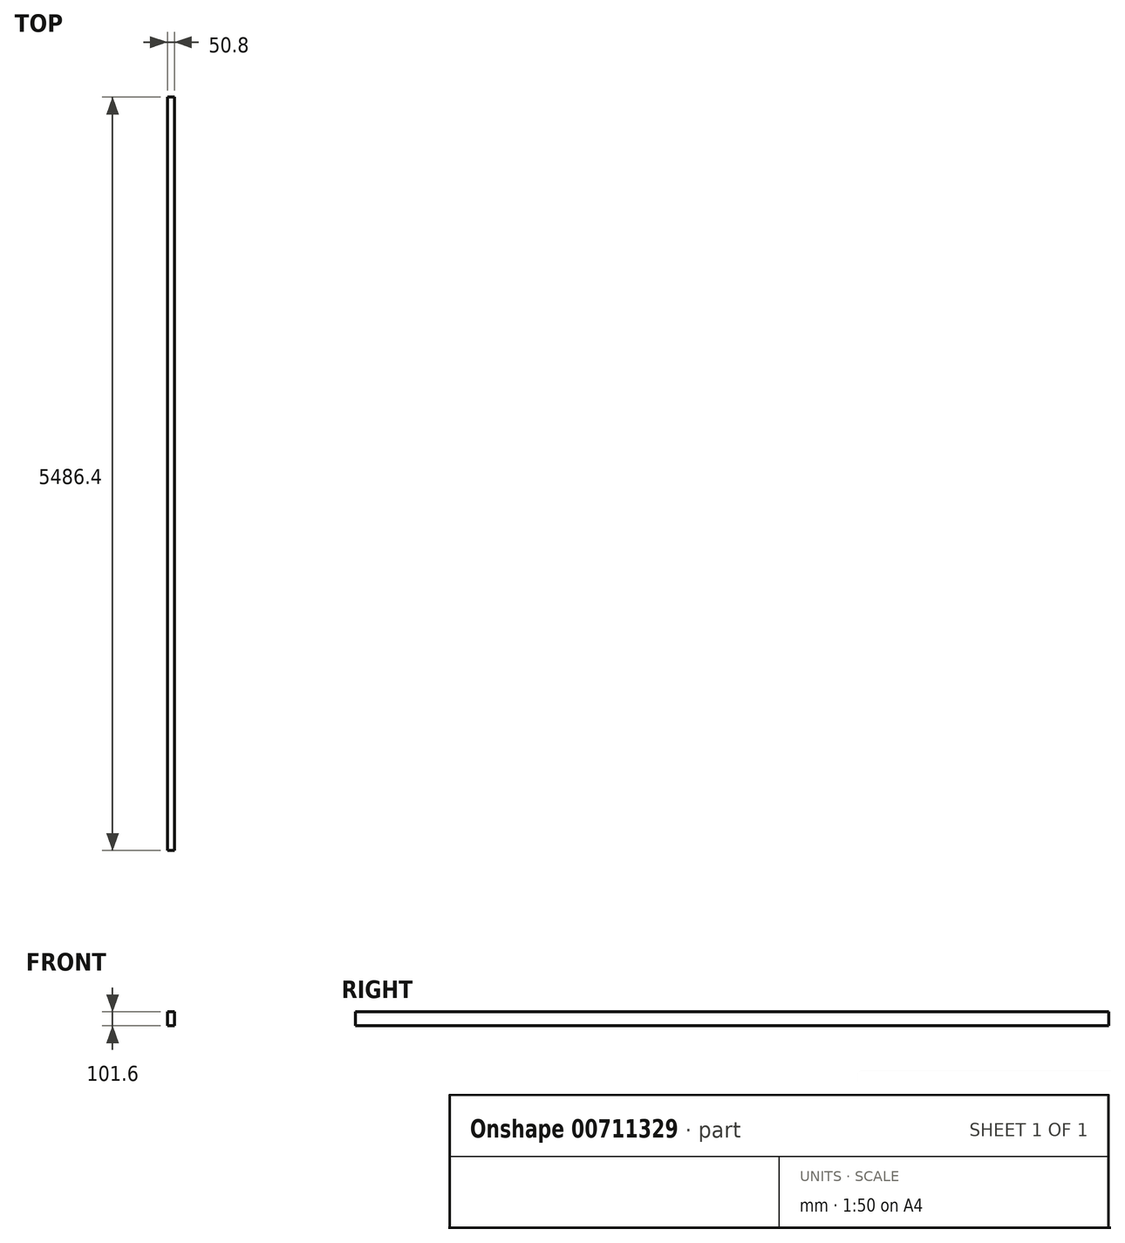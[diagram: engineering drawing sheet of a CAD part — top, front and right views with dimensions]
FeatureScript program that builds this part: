
annotation { "Feature Type Name" : "Feature", "Feature Type Description" : "" }
export const myFeature = defineFeature(function(context is Context, id is Id, definition is map)
    precondition{}
    {
        {
            var Q0;
            Q0=qCreatedBy(makeId("Front.planeOp"),FACE);
            var sketch = newSketch(context, id + "F0", { "sketchPlane" : qUnion([Q0])});
            skLineSegment(sketch, "E0.bottom", {"start": v(25.4, 50.8) * mm, "end": v(-25.4, 50.8) * mm});
            skLineSegment(sketch, "E0.top", {"start": v(25.4, -50.8) * mm, "end": v(-25.4, -50.8) * mm});
            skLineSegment(sketch, "E0.left", {"start": v(25.4, 50.8) * mm, "end": v(25.4, -50.8) * mm});
            skLineSegment(sketch, "E0.right", {"start": v(-25.4, 50.8) * mm, "end": v(-25.4, -50.8) * mm});
            skPoint(sketch, "E0.middle", {"position": v(0, 0) * mm});
            skSolve(sketch);
        }
        {
            var Q0;
            Q0 = qSketchRegion(id + "F0", true);
            extrude(context, id + "F1", {"entities" : qUnion([Q0]), "depth" : 5486.4 * mm, "offsetDistance" : 25.4 * mm});
        }
    });
